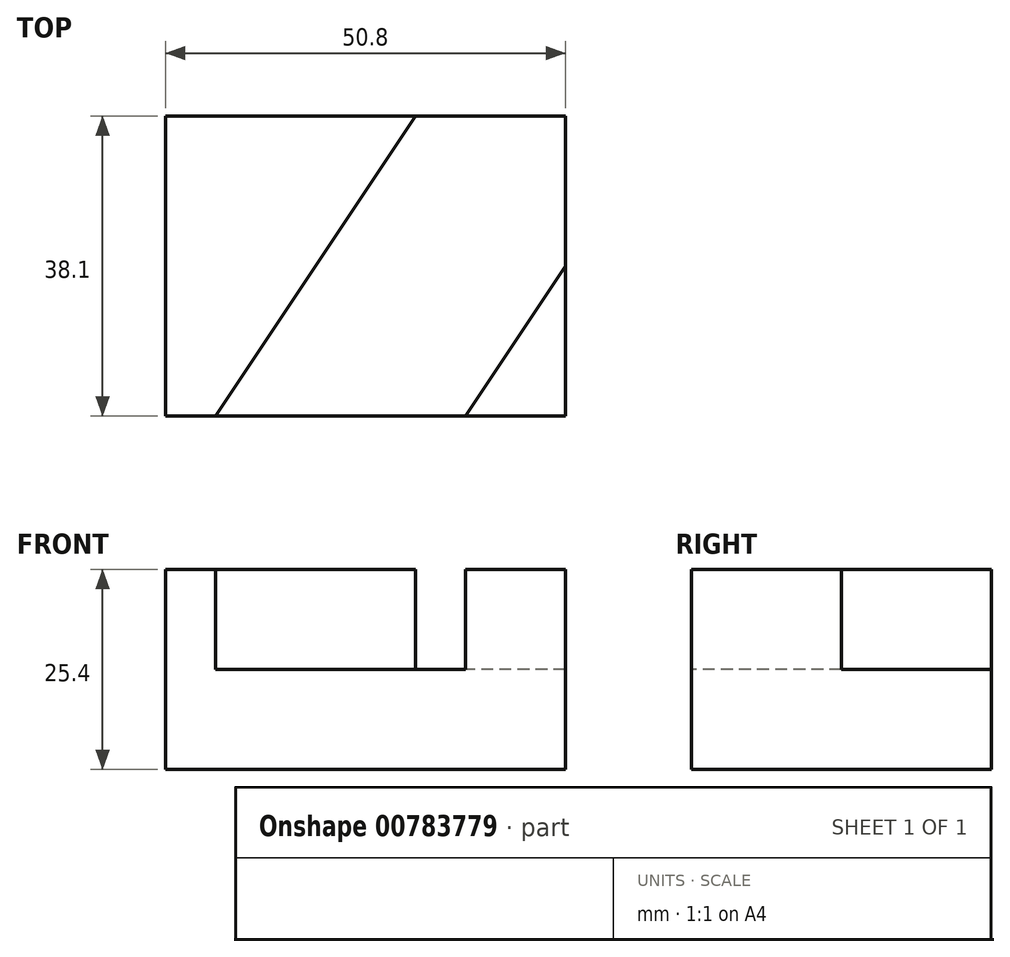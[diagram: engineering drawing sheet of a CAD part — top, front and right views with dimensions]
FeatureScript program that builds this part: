
annotation { "Feature Type Name" : "Feature", "Feature Type Description" : "" }
export const myFeature = defineFeature(function(context is Context, id is Id, definition is map)
    precondition{}
    {
        {
            var Q0;
            Q0=qCreatedBy(makeId("Front.planeOp"),FACE);
            var sketch = newSketch(context, id + "F0", { "sketchPlane" : qUnion([Q0])});
            skLineSegment(sketch, "E0", {"start": v(50.8, 0) * mm, "end": v(0, 0) * mm});
            skLineSegment(sketch, "E1", {"start": v(0, 0) * mm, "end": v(0, -25.4) * mm});
            skLineSegment(sketch, "E2", {"start": v(0, -25.4) * mm, "end": v(50.8, -25.4) * mm});
            skLineSegment(sketch, "E3", {"start": v(50.8, -25.4) * mm, "end": v(50.8, 0) * mm});
            skSolve(sketch);
        }
        {
            var Q0;
            Q0 = qSketchRegion(id + "F0", true);
            extrude(context, id + "F1", {"entities" : qUnion([Q0]), "depth" : 38.1 * mm, "offsetDistance" : 25.4 * mm});
        }
        {
            var Q0;
            Q0=makeQuery(id+"F1.opExtrude","SWEPT_FACE",FACE,{"disambiguationData":[OSD([sQuery(id+"F0.wireOp",EDGE,"E0")])]});
            var sketch = newSketch(context, id + "F2", { "sketchPlane" : qUnion([Q0])});
            skLineSegment(sketch, "E4", {"start": v(0, -38.1) * mm, "end": v(6.35, -38.1) * mm});
            skLineSegment(sketch, "E5", {"start": v(50.8, -38.1) * mm, "end": v(38.1, -38.1) * mm});
            skLineSegment(sketch, "E6", {"start": v(50.8, -38.1) * mm, "end": v(50.8, -19.05) * mm});
            skLineSegment(sketch, "E7", {"start": v(50.8, -19.05) * mm, "end": v(38.1, -38.1) * mm});
            skLineSegment(sketch, "E8", {"start": v(50.8, 0) * mm, "end": v(31.75, 0) * mm});
            skLineSegment(sketch, "E9", {"start": v(31.75, 0) * mm, "end": v(6.35, -38.1) * mm});
            skSolve(sketch);
        }
        {
            var Q0;
            Q0 = qSketchRegion(id + "F2", true);
            var Q1;
            {var subQ3=sQuery(id+"F2.wireOp",EDGE,"E7");Q1=makeQuery(id+"F2.imprint","IMPRINT",FACE,{"disambiguationData":[TD([[makeQuery(id+"F2.imprint","IMPRINT",EDGE,{"derivedFrom":subQ3}),-1.0]])]});}
            extrude(context, id + "F3", {"entities" : qUnion([Q0, Q1]), "operationType" : NewBodyOperationType.REMOVE, "oppositeDirection" : true, "depth" : 12.7 * mm, "offsetDistance" : 25.4 * mm});
        }
        {
            var Q0;
            Q0=makeQuery(id+"F3.boolean.opBoolean","COPY",FACE,{"derivedFrom":makeQuery(id+"F3.opExtrude","CAP_FACE",FACE,{"disambiguationData":[OSD([sQuery(id+"F0.wireOp",EDGE,"E0"),sQuery(id+"F0.wireOp",EDGE,"E3"),sQuery(id+"F2.wireOp",EDGE,"E5"),sQuery(id+"F2.wireOp",EDGE,"E6"),sQuery(id+"F2.wireOp",EDGE,"E8"),sQuery(id+"F2.wireOp",EDGE,"E9")])],"isStart":false})});
            var sketch = newSketch(context, id + "F4", { "sketchPlane" : qUnion([Q0])});
            skLineSegment(sketch, "E10", {"start": v(50.8, -38.1) * mm, "end": v(38.1, -38.1) * mm});
            skLineSegment(sketch, "E11", {"start": v(50.8, -38.1) * mm, "end": v(50.8, -19.05) * mm});
            skLineSegment(sketch, "E12", {"start": v(50.8, -19.05) * mm, "end": v(38.1, -38.1) * mm});
            skSolve(sketch);
        }
        {
            var Q0;
            Q0 = qSketchRegion(id + "F4", true);
            extrude(context, id + "F5", {"entities" : qUnion([Q0]), "operationType" : NewBodyOperationType.ADD, "depth" : 12.7 * mm, "offsetDistance" : 25.4 * mm});
        }
    });
